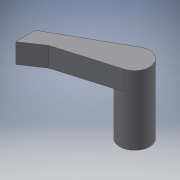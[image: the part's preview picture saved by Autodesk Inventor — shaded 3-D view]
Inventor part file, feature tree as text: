
AUTODESK INVENTOR PART (.ipt)
format: ipt  version: 2019 (Build 230136000, 136)  size: 108,544 bytes
history: native  units: in
note: dims shown in document units (in); Inventor stores cm internally (conversion verified against a paired STEP export)
features: other x3, extrude x2, sketch x2, reference x2
ambient origin geometry x8: Origin, YZ Plane, XZ Plane, XY Plane, X Axis, Y Axis, Z Axis, Center Point
bodies: Solid1 (feature_tree)
feature tree (9):
  extrude  "Extrusion1"  Depth=0.0787in
  extrude  "Extrusion2"  Depth=0.1969in
  sketch  "Sketch1"  dims[d0=0.0787in d1=0.0in d2=0.1181in]
  reference  "Reference1"
  reference  "Reference2"
  sketch  "Sketch2"  dims[d4=0.0787in d7=0.2962in d8=0.1788in d9=0.3848in d10=0.0787in d11=0.1969in d12=0.0in]
  other  "<userpath>\Documents\IQC\CameraSetup.iam"
  other  "CameraSetup.iam"
  other  "Pinion:1"
